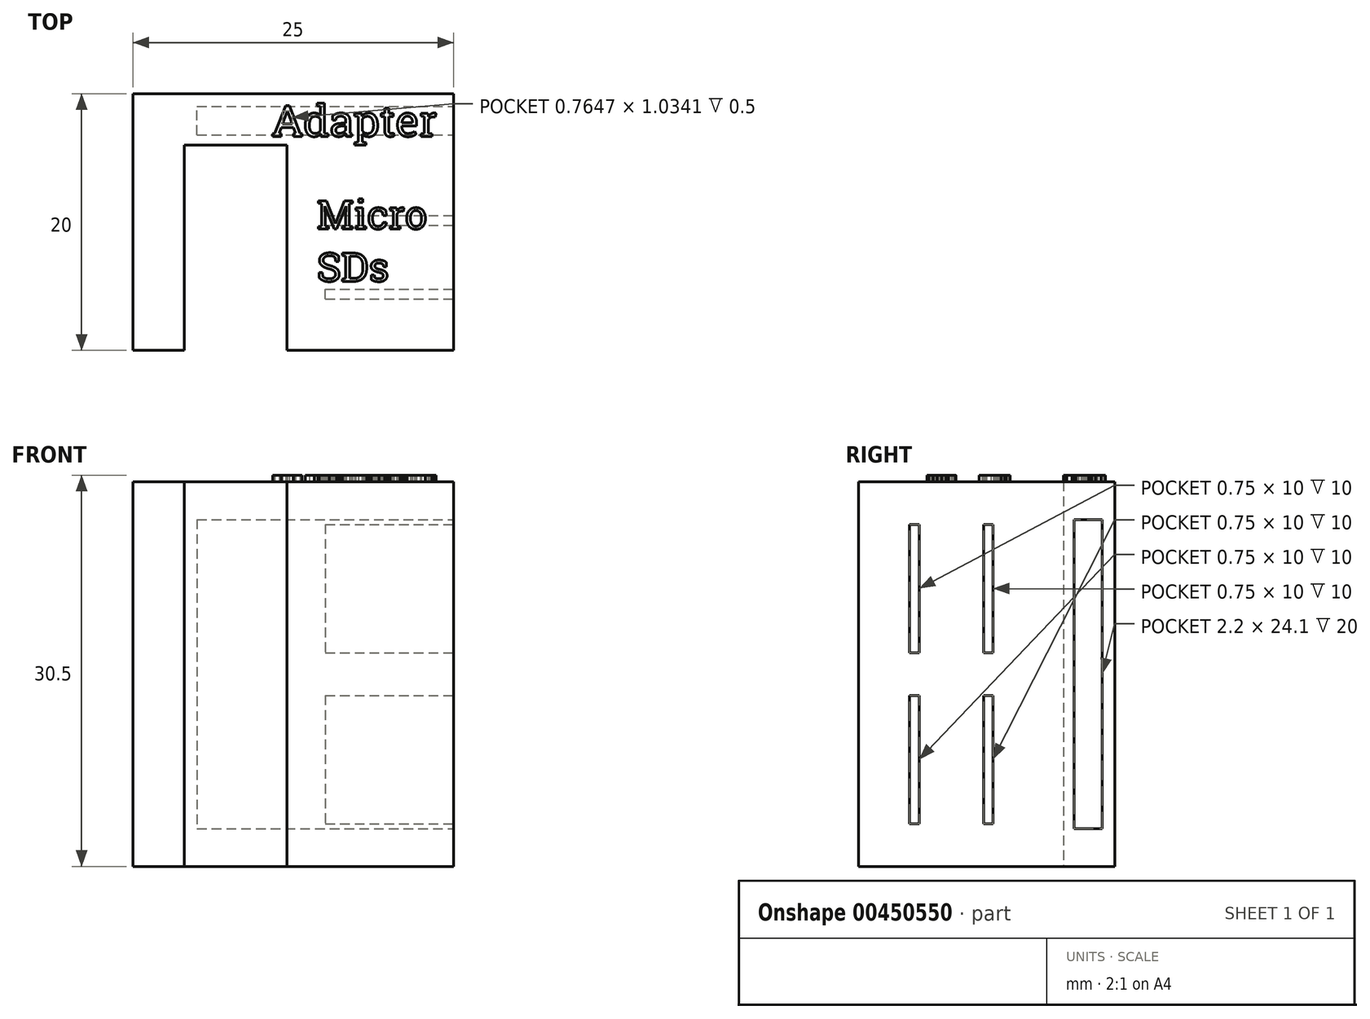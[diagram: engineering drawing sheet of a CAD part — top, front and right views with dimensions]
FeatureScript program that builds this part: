
annotation { "Feature Type Name" : "Feature", "Feature Type Description" : "" }
export const myFeature = defineFeature(function(context is Context, id is Id, definition is map)
    precondition{}
    {
        {
            var Q0;
            Q0=qCreatedBy(makeId("Top.planeOp"),FACE);
            var sketch = newSketch(context, id + "F0", { "sketchPlane" : qUnion([Q0])});
            skLineSegment(sketch, "E0.bottom", {"start": v(0, 0) * mm, "end": v(4, 0) * mm});
            skLineSegment(sketch, "E0.top", {"start": v(0, 20) * mm, "end": v(25, 20) * mm});
            skLineSegment(sketch, "E0.left", {"start": v(0, 0) * mm, "end": v(0, 20) * mm});
            skLineSegment(sketch, "E0.right", {"start": v(25, 0) * mm, "end": v(25, 20) * mm});
            skLineSegment(sketch, "E1", {"start": v(4, 0) * mm, "end": v(4, 16) * mm});
            skLineSegment(sketch, "E2", {"start": v(4, 16) * mm, "end": v(12, 16) * mm});
            skLineSegment(sketch, "E3", {"start": v(12, 16) * mm, "end": v(12, 0) * mm});
            skLineSegment(sketch, "E4.trimOffspring", {"start": v(12, 0) * mm, "end": v(25, 0) * mm});
            skSolve(sketch);
        }
        {
            var Q0;
            Q0 = qSketchRegion(id + "F0", true);
            extrude(context, id + "F1", {"entities" : qUnion([Q0]), "depth" : 30 * mm});
        }
        {
            var Q0;
            Q0=makeQuery(id+"F1.opExtrude","SWEPT_FACE",FACE,{"disambiguationData":[OSD([sQuery(id+"F0.wireOp",EDGE,"E0.right")])]});
            var sketch = newSketch(context, id + "F2", { "sketchPlane" : qUnion([Q0])});
            skLineSegment(sketch, "E5.bottom", {"start": v(4, 26.67) * mm, "end": v(4.75, 26.67) * mm});
            skLineSegment(sketch, "E5.top", {"start": v(4, 16.67) * mm, "end": v(4.75, 16.67) * mm});
            skLineSegment(sketch, "E5.left", {"start": v(4, 26.67) * mm, "end": v(4, 16.67) * mm});
            skLineSegment(sketch, "E5.right", {"start": v(4.75, 26.67) * mm, "end": v(4.75, 16.67) * mm});
            skLineSegment(sketch, "E6.bottom", {"start": v(9.75, 26.67) * mm, "end": v(10.5, 26.67) * mm});
            skLineSegment(sketch, "E6.top", {"start": v(9.75, 16.67) * mm, "end": v(10.5, 16.67) * mm});
            skLineSegment(sketch, "E6.left", {"start": v(9.75, 26.67) * mm, "end": v(9.75, 16.67) * mm});
            skLineSegment(sketch, "E6.right", {"start": v(10.5, 26.67) * mm, "end": v(10.5, 16.67) * mm});
            skLineSegment(sketch, "E7.bottom", {"start": v(4, 13.33) * mm, "end": v(4.75, 13.33) * mm});
            skLineSegment(sketch, "E7.top", {"start": v(4, 3.33) * mm, "end": v(4.75, 3.33) * mm});
            skLineSegment(sketch, "E7.left", {"start": v(4, 13.33) * mm, "end": v(4, 3.33) * mm});
            skLineSegment(sketch, "E7.right", {"start": v(4.75, 13.33) * mm, "end": v(4.75, 3.33) * mm});
            skLineSegment(sketch, "E8.bottom", {"start": v(9.75, 13.33) * mm, "end": v(10.5, 13.33) * mm});
            skLineSegment(sketch, "E8.top", {"start": v(9.75, 3.33) * mm, "end": v(10.5, 3.33) * mm});
            skLineSegment(sketch, "E8.left", {"start": v(9.75, 13.33) * mm, "end": v(9.75, 3.33) * mm});
            skLineSegment(sketch, "E8.right", {"start": v(10.5, 13.33) * mm, "end": v(10.5, 3.33) * mm});
            skSolve(sketch);
        }
        {
            var Q0;
            Q0 = qSketchRegion(id + "F2", true);
            extrude(context, id + "F3", {"entities" : qUnion([Q0]), "operationType" : NewBodyOperationType.REMOVE, "oppositeDirection" : true, "depth" : 10 * mm});
        }
        {
            var Q0;
            Q0=makeQuery(id+"F1.opExtrude","SWEPT_FACE",FACE,{"disambiguationData":[OSD([sQuery(id+"F0.wireOp",EDGE,"E0.right")])]});
            var sketch = newSketch(context, id + "F4", { "sketchPlane" : qUnion([Q0])});
            skLineSegment(sketch, "E9.bottom", {"start": v(16.8, 27.05) * mm, "end": v(19, 27.05) * mm});
            skLineSegment(sketch, "E9.top", {"start": v(16.8, 2.95) * mm, "end": v(19, 2.95) * mm});
            skLineSegment(sketch, "E9.left", {"start": v(16.8, 27.05) * mm, "end": v(16.8, 2.95) * mm});
            skLineSegment(sketch, "E9.right", {"start": v(19, 27.05) * mm, "end": v(19, 2.95) * mm});
            skSolve(sketch);
        }
        {
            var Q0;
            Q0 = qSketchRegion(id + "F4", true);
            extrude(context, id + "F5", {"entities" : qUnion([Q0]), "operationType" : NewBodyOperationType.REMOVE, "oppositeDirection" : true, "depth" : 20 * mm});
        }
        {
            var Q0;
            Q0=makeQuery(id+"F1.opExtrude","CAP_FACE",FACE,{"disambiguationData":[OSD([sQuery(id+"F0.wireOp",EDGE,"E0.bottom"),sQuery(id+"F0.wireOp",EDGE,"E0.top"),sQuery(id+"F0.wireOp",EDGE,"E0.left"),sQuery(id+"F0.wireOp",EDGE,"E0.right"),sQuery(id+"F0.wireOp",EDGE,"E1"),sQuery(id+"F0.wireOp",EDGE,"E2"),sQuery(id+"F0.wireOp",EDGE,"E3"),sQuery(id+"F0.wireOp",EDGE,"E4.trimOffspring")])],"isStart":false});
            var sketch = newSketch(context, id + "F6", { "sketchPlane" : qUnion([Q0])});
            skText(sketch, "E10", { "text": "Micro\nSDs", "fontName": "RobotoSlab-Regular.ttf"});
            skText(sketch, "E11", { "text": "Adapter", "fontName": "RobotoSlab-Regular.ttf"});
            const initialGuessF6  = {"E10": [0.01435, 0.00946, 1, 0, 0.00223], "E11": [0.0108, 0.01668, 1, 0, 0.00244]};
            skSetInitialGuess(sketch, initialGuessF6);
            skSolve(sketch);
        }
        {
            var Q0;
            Q0 = qSketchRegion(id + "F6", true);
            extrude(context, id + "F7", {"entities" : qUnion([Q0]), "operationType" : NewBodyOperationType.ADD, "depth" : .5 * mm});
        }
    });
